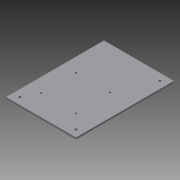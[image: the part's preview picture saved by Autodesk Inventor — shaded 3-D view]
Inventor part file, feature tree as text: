
AUTODESK INVENTOR PART (.ipt)
format: ipt  version: 2014 (Build 180170000, 170)  size: 98,304 bytes
history: native  units: in
note: dims shown in document units (in); Inventor stores cm internally (conversion verified against a paired STEP export)
features: hole x2, other x2, extrude x1, imported_body x1
ambient origin geometry x8: Origin, YZ Plane, XZ Plane, XY Plane, X Axis, Y Axis, Z Axis, Center Point
bodies: Body1 (feature_tree)
feature tree (6):
  extrude  "Base 1/8""  Depth=5.0in
  hole  "TopLayerHoles"  [1 undecoded]
  hole  "ControllerHoles"  [1 undecoded]
  imported_body  "Base"
  other  "TopLayer"
  other  "Controller"
note: 2 required parameter values undecoded (feature->parameter linkage not recoverable at this tier; creation-order binding heuristic only, values carry confidence <= 0.55)
